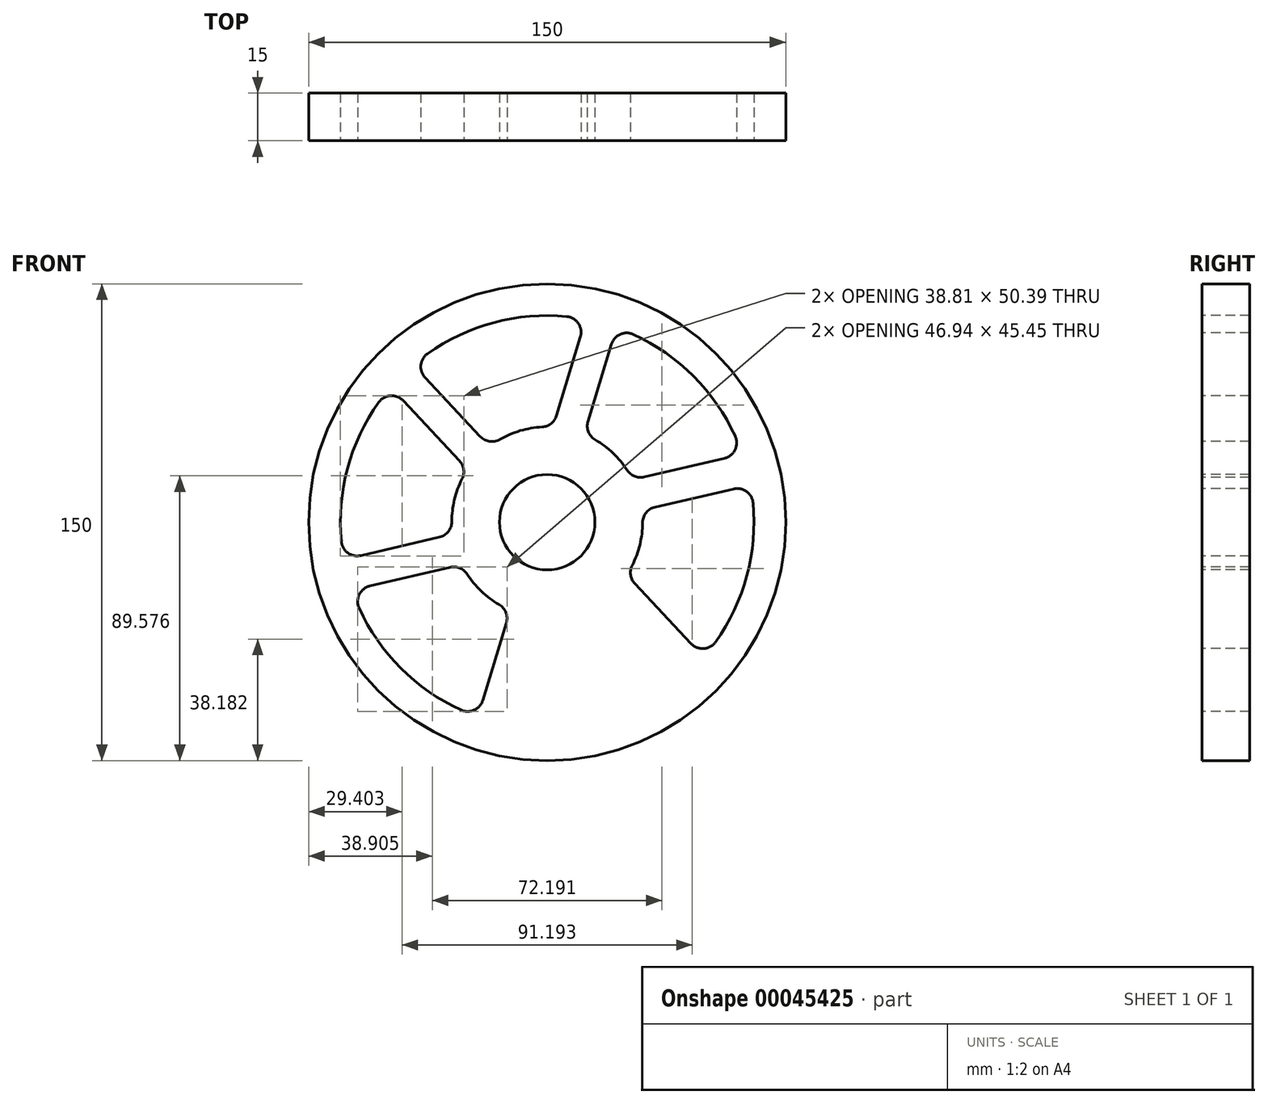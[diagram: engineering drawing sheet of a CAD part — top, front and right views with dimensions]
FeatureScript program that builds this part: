
annotation { "Feature Type Name" : "Feature", "Feature Type Description" : "" }
export const myFeature = defineFeature(function(context is Context, id is Id, definition is map)
    precondition{}
    {
        {
            var Q0;
            Q0=qCreatedBy(makeId("Front.planeOp"),FACE);
            var sketch = newSketch(context, id + "F0", { "sketchPlane" : qUnion([Q0])});
            skCircle(sketch, "E0", {"center": v(0, 0) * mm, "radius": 75 * mm});
            skCircle(sketch, "E1", {"center": v(0, 0) * mm, "radius": 15 * mm});
            skSolve(sketch);
        }
        {
            var Q0;
            Q0 = qSketchRegion(id + "F0", true);
            extrude(context, id + "F1", {"entities" : qUnion([Q0]), "oppositeDirection" : true, "depth" : 15 * mm});
        }
        {
            var Q0;
            Q0=makeQuery(id+"F1.opExtrude","CAP_FACE",FACE,{"disambiguationData":[OSD([sQuery(id+"F0.wireOp",EDGE,"E0"),sQuery(id+"F0.wireOp",EDGE,"E1")])],"isStart":true});
            var sketch = newSketch(context, id + "F2", { "sketchPlane" : qUnion([Q0])});
            skCircle(sketch, "E2", {"center": v(0, 0) * mm, "radius": 30 * mm});
            skCircle(sketch, "E3", {"center": v(0, 0) * mm, "radius": 65 * mm});
            skLineSegment(sketch, "E4", {"start": v(1.85, 29.94) * mm, "end": v(12.15, 63.85) * mm});
            skLineSegment(sketch, "E5", {"start": v(11.61, 27.66) * mm, "end": v(21.8, 61.23) * mm});
            skLineSegment(sketch, "E6.1.0", {"start": v(29.76, 3.77) * mm, "end": v(63.93, 11.73) * mm});
            skLineSegment(sketch, "E6.1.1", {"start": v(26.86, 13.37) * mm, "end": v(61.38, 21.4) * mm});
            skLineSegment(sketch, "E6.2.0", {"start": v(18.15, -23.89) * mm, "end": v(42.12, -49.5) * mm});
            skLineSegment(sketch, "E6.2.1", {"start": v(25, -16.58) * mm, "end": v(49.22, -42.45) * mm});
            skLineSegment(sketch, "E7.1.0", {"start": v(-26.86, -13.37) * mm, "end": v(-61.38, -21.4) * mm});
            skLineSegment(sketch, "E7.1.1", {"start": v(-29.76, -3.77) * mm, "end": v(-63.93, -11.73) * mm});
            skLineSegment(sketch, "E7.1.2", {"start": v(-25, 16.58) * mm, "end": v(-49.22, 42.45) * mm});
            skLineSegment(sketch, "E7.1.3", {"start": v(-18.15, 23.89) * mm, "end": v(-42.12, 49.5) * mm});
            skLineSegment(sketch, "E7.2.2", {"start": v(-1.85, -29.94) * mm, "end": v(-12.15, -63.85) * mm});
            skLineSegment(sketch, "E7.2.3", {"start": v(-11.61, -27.66) * mm, "end": v(-21.8, -61.23) * mm});
            skSolve(sketch);
        }
        {
            var Q0;
            {var subQ0=sQuery(id+"F2.wireOp",EDGE,"E7.1.1");Q0=makeQuery(id+"F2.imprint","IMPRINT",FACE,{"disambiguationData":[TD([[makeQuery(id+"F2.imprint","IMPRINT",EDGE,{"derivedFrom":subQ0}),-1.0]])]});}
            var Q1;
            {var subQ2=sQuery(id+"F2.wireOp",EDGE,"E4");Q1=makeQuery(id+"F2.imprint","IMPRINT",FACE,{"disambiguationData":[TD([[makeQuery(id+"F2.imprint","IMPRINT",EDGE,{"derivedFrom":subQ2}),1.0]])]});}
            var Q2;
            {var subQ1=sQuery(id+"F2.wireOp",EDGE,"E5");Q2=makeQuery(id+"F2.imprint","IMPRINT",FACE,{"disambiguationData":[TD([[makeQuery(id+"F2.imprint","IMPRINT",EDGE,{"derivedFrom":subQ1}),-1.0]])]});}
            var Q3;
            {var subQ2=sQuery(id+"F2.wireOp",EDGE,"E6.1.0");Q3=makeQuery(id+"F2.imprint","IMPRINT",FACE,{"disambiguationData":[TD([[makeQuery(id+"F2.imprint","IMPRINT",EDGE,{"derivedFrom":subQ2}),-1.0]])]});}
            var Q4;
            {var subQ2=sQuery(id+"F2.wireOp",EDGE,"E6.2.0");Q4=makeQuery(id+"F2.imprint","IMPRINT",FACE,{"disambiguationData":[TD([[makeQuery(id+"F2.imprint","IMPRINT",EDGE,{"derivedFrom":subQ2}),-1.0]])]});}
            var Q5;
            {var subQ2=sQuery(id+"F2.wireOp",EDGE,"E7.1.0");Q5=makeQuery(id+"F2.imprint","IMPRINT",FACE,{"disambiguationData":[TD([[makeQuery(id+"F2.imprint","IMPRINT",EDGE,{"derivedFrom":subQ2}),1.0]])]});}
            extrude(context, id + "F3", {"entities" : qUnion([Q0, Q1, Q2, Q3, Q4, Q5]), "operationType" : NewBodyOperationType.REMOVE, "oppositeDirection" : true, "depth" : 25 * mm});
        }
        {
            var Q0;
            Q0=makeQuery(id+"F3.boolean.opBoolean","COPY",EDGE,{"derivedFrom":makeQuery(id+"F3.opExtrude","SWEPT_EDGE",EDGE,{"disambiguationData":[OSD([sQuery(id+"F2.wireOp",EDGE,"E3"),sQuery(id+"F2.wireOp",EDGE,"E7.1.1")])]})});
            var Q1;
            Q1=makeQuery(id+"F3.boolean.opBoolean","COPY",EDGE,{"derivedFrom":makeQuery(id+"F3.opExtrude","SWEPT_EDGE",EDGE,{"disambiguationData":[OSD([sQuery(id+"F2.wireOp",EDGE,"E3"),sQuery(id+"F2.wireOp",EDGE,"E7.1.2")])]})});
            var Q2;
            Q2=makeQuery(id+"F3.boolean.opBoolean","COPY",EDGE,{"derivedFrom":makeQuery(id+"F3.opExtrude","SWEPT_EDGE",EDGE,{"disambiguationData":[OSD([sQuery(id+"F2.wireOp",EDGE,"E3"),sQuery(id+"F2.wireOp",EDGE,"E4")])]})});
            var Q3;
            Q3=makeQuery(id+"F3.boolean.opBoolean","COPY",EDGE,{"derivedFrom":makeQuery(id+"F3.opExtrude","SWEPT_EDGE",EDGE,{"disambiguationData":[OSD([sQuery(id+"F2.wireOp",EDGE,"E3"),sQuery(id+"F2.wireOp",EDGE,"E7.1.3")])]})});
            var Q4;
            Q4=makeQuery(id+"F3.boolean.opBoolean","COPY",EDGE,{"derivedFrom":makeQuery(id+"F3.opExtrude","SWEPT_EDGE",EDGE,{"disambiguationData":[OSD([sQuery(id+"F2.wireOp",EDGE,"E3"),sQuery(id+"F2.wireOp",EDGE,"E5")])]})});
            var Q5;
            Q5=makeQuery(id+"F3.boolean.opBoolean","COPY",EDGE,{"derivedFrom":makeQuery(id+"F3.opExtrude","SWEPT_EDGE",EDGE,{"disambiguationData":[OSD([sQuery(id+"F2.wireOp",EDGE,"E3"),sQuery(id+"F2.wireOp",EDGE,"E6.1.1")])]})});
            var Q6;
            Q6=makeQuery(id+"F3.boolean.opBoolean","COPY",EDGE,{"derivedFrom":makeQuery(id+"F3.opExtrude","SWEPT_EDGE",EDGE,{"disambiguationData":[OSD([sQuery(id+"F2.wireOp",EDGE,"E3"),sQuery(id+"F2.wireOp",EDGE,"E6.1.0")])]})});
            var Q7;
            Q7=makeQuery(id+"F3.boolean.opBoolean","COPY",EDGE,{"derivedFrom":makeQuery(id+"F3.opExtrude","SWEPT_EDGE",EDGE,{"disambiguationData":[OSD([sQuery(id+"F2.wireOp",EDGE,"E3"),sQuery(id+"F2.wireOp",EDGE,"E6.2.1")])]})});
            var Q8;
            Q8=makeQuery(id+"F3.boolean.opBoolean","COPY",EDGE,{"derivedFrom":makeQuery(id+"F3.opExtrude","SWEPT_EDGE",EDGE,{"disambiguationData":[OSD([sQuery(id+"F2.wireOp",EDGE,"E3"),sQuery(id+"F2.wireOp",EDGE,"E6.2.0")])]})});
            var Q9;
            Q9=makeQuery(id+"F3.boolean.opBoolean","COPY",EDGE,{"derivedFrom":makeQuery(id+"F3.opExtrude","SWEPT_EDGE",EDGE,{"disambiguationData":[OSD([sQuery(id+"F2.wireOp",EDGE,"E3"),sQuery(id+"F2.wireOp",EDGE,"E7.2.2")])]})});
            var Q10;
            Q10=makeQuery(id+"F3.boolean.opBoolean","COPY",EDGE,{"derivedFrom":makeQuery(id+"F3.opExtrude","SWEPT_EDGE",EDGE,{"disambiguationData":[OSD([sQuery(id+"F2.wireOp",EDGE,"E3"),sQuery(id+"F2.wireOp",EDGE,"E7.2.3")])]})});
            var Q11;
            Q11=makeQuery(id+"F3.boolean.opBoolean","COPY",EDGE,{"derivedFrom":makeQuery(id+"F3.opExtrude","SWEPT_EDGE",EDGE,{"disambiguationData":[OSD([sQuery(id+"F2.wireOp",EDGE,"E3"),sQuery(id+"F2.wireOp",EDGE,"E7.1.0")])]})});
            fillet(context, id + "F4", {"entities" : qUnion([Q0, Q1, Q2, Q3, Q4, Q5, Q6, Q7, Q8, Q9, Q10, Q11]), "radius" : 5 * mm, "tangentPropagation" : true, "allowEdgeOverflow" : false});
        }
        {
            var Q0;
            Q0=makeQuery(id+"F3.boolean.opBoolean","COPY",EDGE,{"derivedFrom":makeQuery(id+"F3.opExtrude","SWEPT_EDGE",EDGE,{"disambiguationData":[OSD([sQuery(id+"F2.wireOp",EDGE,"E2"),sQuery(id+"F2.wireOp",EDGE,"E6.2.1")])]})});
            var Q1;
            Q1=makeQuery(id+"F3.boolean.opBoolean","COPY",EDGE,{"derivedFrom":makeQuery(id+"F3.opExtrude","SWEPT_EDGE",EDGE,{"disambiguationData":[OSD([sQuery(id+"F2.wireOp",EDGE,"E2"),sQuery(id+"F2.wireOp",EDGE,"E6.1.0")])]})});
            var Q2;
            Q2=makeQuery(id+"F3.boolean.opBoolean","COPY",EDGE,{"derivedFrom":makeQuery(id+"F3.opExtrude","SWEPT_EDGE",EDGE,{"disambiguationData":[OSD([sQuery(id+"F2.wireOp",EDGE,"E2"),sQuery(id+"F2.wireOp",EDGE,"E7.2.2")])]})});
            var Q3;
            Q3=makeQuery(id+"F3.boolean.opBoolean","COPY",EDGE,{"derivedFrom":makeQuery(id+"F3.opExtrude","SWEPT_EDGE",EDGE,{"disambiguationData":[OSD([sQuery(id+"F2.wireOp",EDGE,"E2"),sQuery(id+"F2.wireOp",EDGE,"E7.2.3")])]})});
            var Q4;
            Q4=makeQuery(id+"F3.boolean.opBoolean","COPY",EDGE,{"derivedFrom":makeQuery(id+"F3.opExtrude","SWEPT_EDGE",EDGE,{"disambiguationData":[OSD([sQuery(id+"F2.wireOp",EDGE,"E2"),sQuery(id+"F2.wireOp",EDGE,"E7.1.0")])]})});
            var Q5;
            Q5=makeQuery(id+"F3.boolean.opBoolean","COPY",EDGE,{"derivedFrom":makeQuery(id+"F3.opExtrude","SWEPT_EDGE",EDGE,{"disambiguationData":[OSD([sQuery(id+"F2.wireOp",EDGE,"E2"),sQuery(id+"F2.wireOp",EDGE,"E7.1.1")])]})});
            var Q6;
            Q6=makeQuery(id+"F3.boolean.opBoolean","COPY",EDGE,{"derivedFrom":makeQuery(id+"F3.opExtrude","SWEPT_EDGE",EDGE,{"disambiguationData":[OSD([sQuery(id+"F2.wireOp",EDGE,"E2"),sQuery(id+"F2.wireOp",EDGE,"E7.1.2")])]})});
            var Q7;
            Q7=makeQuery(id+"F3.boolean.opBoolean","COPY",EDGE,{"derivedFrom":makeQuery(id+"F3.opExtrude","SWEPT_EDGE",EDGE,{"disambiguationData":[OSD([sQuery(id+"F2.wireOp",EDGE,"E2"),sQuery(id+"F2.wireOp",EDGE,"E7.1.3")])]})});
            var Q8;
            Q8=makeQuery(id+"F3.boolean.opBoolean","COPY",EDGE,{"derivedFrom":makeQuery(id+"F3.opExtrude","SWEPT_EDGE",EDGE,{"disambiguationData":[OSD([sQuery(id+"F2.wireOp",EDGE,"E2"),sQuery(id+"F2.wireOp",EDGE,"E4")])]})});
            var Q9;
            Q9=makeQuery(id+"F3.boolean.opBoolean","COPY",EDGE,{"derivedFrom":makeQuery(id+"F3.opExtrude","SWEPT_EDGE",EDGE,{"disambiguationData":[OSD([sQuery(id+"F2.wireOp",EDGE,"E2"),sQuery(id+"F2.wireOp",EDGE,"E5")])]})});
            var Q10;
            Q10=makeQuery(id+"F3.boolean.opBoolean","COPY",EDGE,{"derivedFrom":makeQuery(id+"F3.opExtrude","SWEPT_EDGE",EDGE,{"disambiguationData":[OSD([sQuery(id+"F2.wireOp",EDGE,"E2"),sQuery(id+"F2.wireOp",EDGE,"E6.1.1")])]})});
            fillet(context, id + "F5", {"entities" : qUnion([Q0, Q1, Q2, Q3, Q4, Q5, Q6, Q7, Q8, Q9, Q10]), "radius" : 5 * mm, "tangentPropagation" : true, "allowEdgeOverflow" : false});
        }
    });
